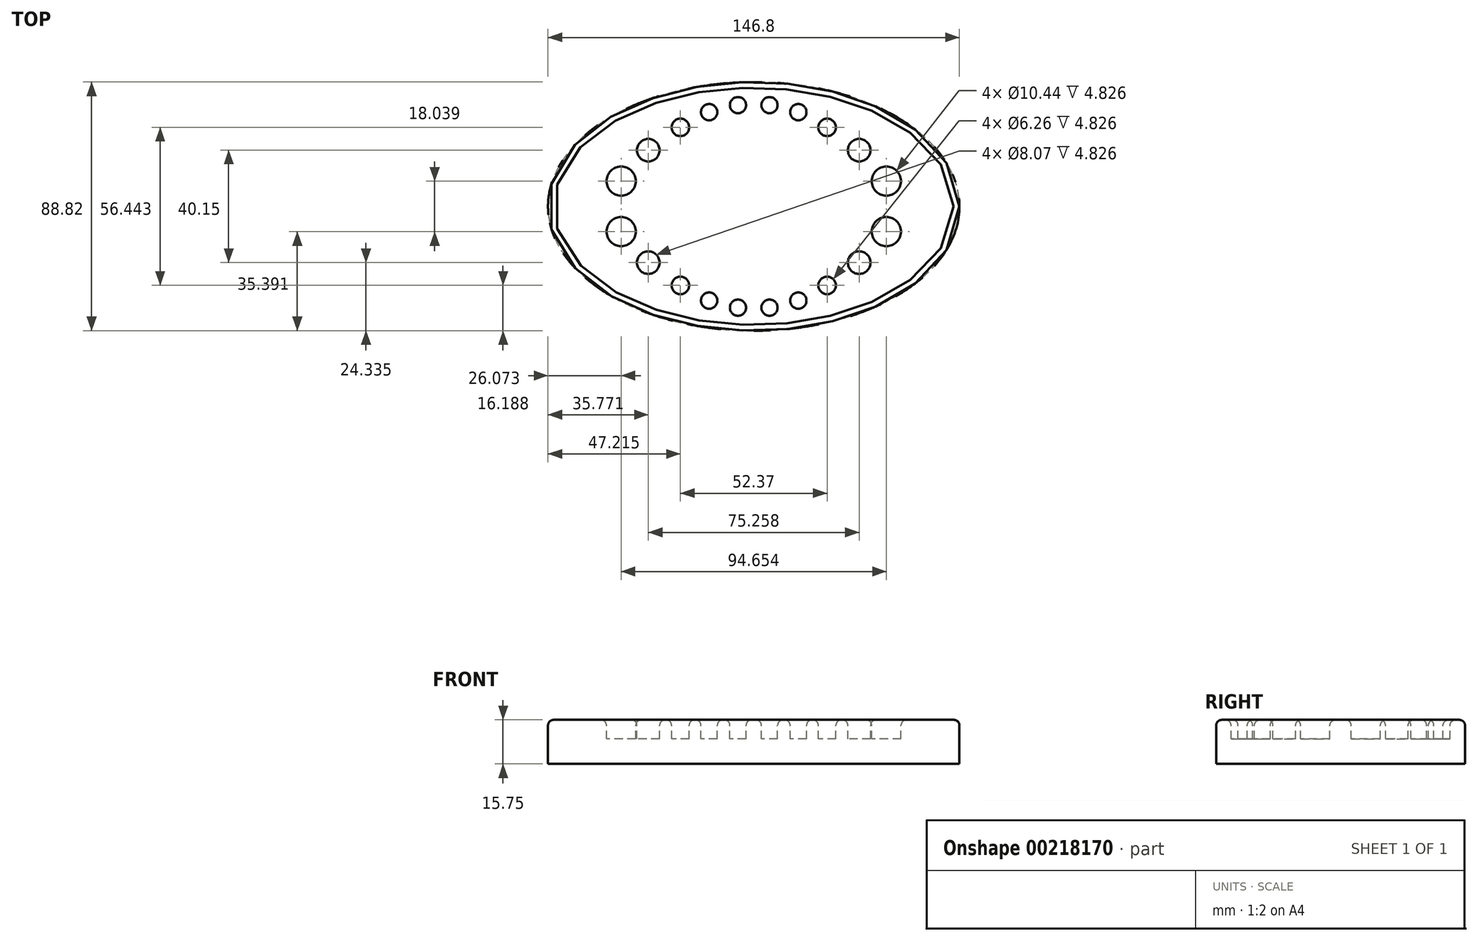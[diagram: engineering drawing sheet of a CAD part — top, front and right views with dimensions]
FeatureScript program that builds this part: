
annotation { "Feature Type Name" : "Feature", "Feature Type Description" : "" }
export const myFeature = defineFeature(function(context is Context, id is Id, definition is map)
    precondition{}
    {
        {
            var Q0;
            Q0=qCreatedBy(makeId("Top.planeOp"),FACE);
            var sketch = newSketch(context, id + "F0", { "sketchPlane" : qUnion([Q0])});
            skCircle(sketch, "E0", {"center": v(-47.33, 9.02) * mm, "radius": 5.22 * mm});
            skCircle(sketch, "E1", {"center": v(-37.63, 20.08) * mm, "radius": 4.04 * mm});
            skCircle(sketch, "E2", {"center": v(-26.19, 28.22) * mm, "radius": 3.13 * mm});
            skCircle(sketch, "E3", {"center": v(-15.9, 33.65) * mm, "radius": 2.9 * mm});
            skCircle(sketch, "E4", {"center": v(-5.62, 36.17) * mm, "radius": 2.88 * mm});
            skCircle(sketch, "E5.MirrorC", {"center": v(26.19, 28.22) * mm, "radius": 3.13 * mm});
            skCircle(sketch, "E6.MirrorC", {"center": v(5.62, 36.17) * mm, "radius": 2.88 * mm});
            skCircle(sketch, "E7.MirrorC", {"center": v(15.9, 33.65) * mm, "radius": 2.9 * mm});
            skCircle(sketch, "E8.MirrorC", {"center": v(37.63, 20.08) * mm, "radius": 4.04 * mm});
            skCircle(sketch, "E9.MirrorC", {"center": v(47.33, 9.02) * mm, "radius": 5.22 * mm});
            skCircle(sketch, "E10.MirrorC", {"center": v(26.19, -28.22) * mm, "radius": 3.13 * mm});
            skCircle(sketch, "E11.MirrorC", {"center": v(-5.62, -36.17) * mm, "radius": 2.88 * mm});
            skCircle(sketch, "E12.MirrorC", {"center": v(15.9, -33.65) * mm, "radius": 2.9 * mm});
            skCircle(sketch, "E13.MirrorC", {"center": v(-26.19, -28.22) * mm, "radius": 3.13 * mm});
            skCircle(sketch, "E14.MirrorC", {"center": v(-37.63, -20.08) * mm, "radius": 4.04 * mm});
            skCircle(sketch, "E15.MirrorC", {"center": v(47.33, -9.02) * mm, "radius": 5.22 * mm});
            skCircle(sketch, "E16.MirrorC", {"center": v(37.63, -20.08) * mm, "radius": 4.04 * mm});
            skCircle(sketch, "E17.MirrorC", {"center": v(-15.9, -33.65) * mm, "radius": 2.9 * mm});
            skCircle(sketch, "E18.MirrorC", {"center": v(5.62, -36.17) * mm, "radius": 2.88 * mm});
            skCircle(sketch, "E19.MirrorC", {"center": v(-47.33, -9.02) * mm, "radius": 5.22 * mm});
            skSolve(sketch);
        }
        {
            var Q0;
            Q0=qCreatedBy(makeId("Top.planeOp"),FACE);
            var sketch = newSketch(context, id + "F1", { "sketchPlane" : qUnion([Q0])});
            skEllipse(sketch, "E20", {"center": v(0, 0) * mm, "majorRadius": 73.4 * mm, "minorRadius": 44.4 * mm, "majorAxis": v(1, 0)});
            skSolve(sketch);
        }
        {
            var Q0;
            Q0 = qSketchRegion(id + "F1", true);
            extrude(context, id + "F2", {"entities" : qUnion([Q0]), "oppositeDirection" : true, "depth" : 15.75 * mm});
        }
        {
            var Q0;
            Q0 = qSketchRegion(id + "F0", true);
            extrude(context, id + "F3", {"entities" : qUnion([Q0]), "operationType" : NewBodyOperationType.REMOVE, "oppositeDirection" : true, "depth" : 6.86 * mm});
        }
        {
            var Q0;
            Q0=makeQuery(id+"F2.opExtrude","CAP_FACE",FACE,{"disambiguationData":[OSD([sQuery(id+"F1.wireOp",EDGE,"E20")])],"isStart":true});
            fillet(context, id + "F4", {"entities" : qUnion([Q0]), "radius" : 2.03 * mm, "tangentPropagation" : true, "allowEdgeOverflow" : false});
        }
    });
